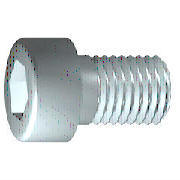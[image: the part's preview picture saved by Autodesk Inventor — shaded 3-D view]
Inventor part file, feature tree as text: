
AUTODESK INVENTOR PART (.ipt)
format: ipt  version: 2022 (Build 260153000, 153)  size: 192,000 bytes
history: native  units: mm (DEFAULTED — no unit token found)
features: sketch x2, other x1, extrude x1, plane x1, fillet x1
ambient origin geometry x7: Origin, YZ Plane, XY Plane, X Axis, Y Axis, Z Axis, Center Point
bodies: Solid1 (feature_tree)
feature tree (6):
  other  "Базовый элемент"
  extrude  "Паз"  Depth=10.65mm
  plane  "Work Plane1"
  fillet  "Fillet2"  Radius=0.276153mm
  sketch  "Эскиз1"
  sketch  "Эскиз2"
